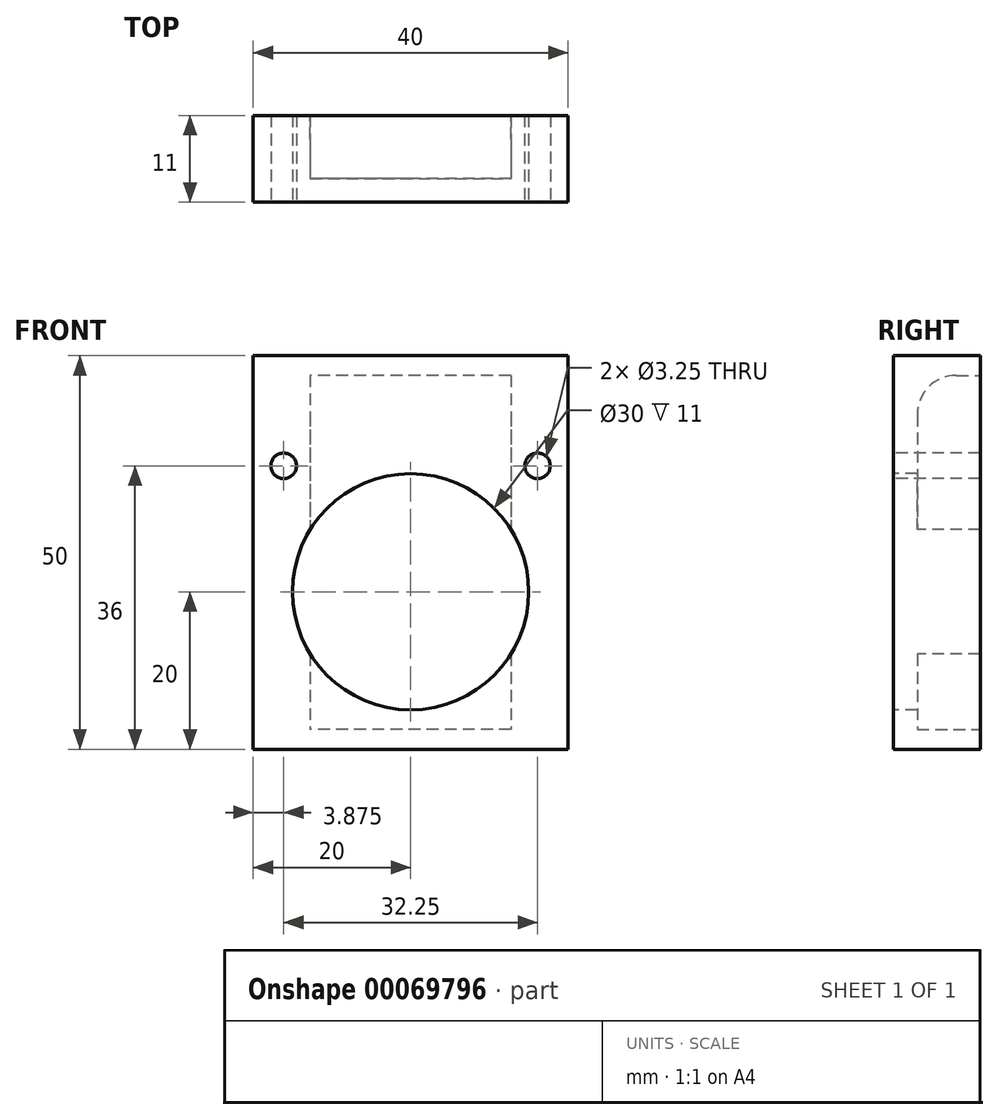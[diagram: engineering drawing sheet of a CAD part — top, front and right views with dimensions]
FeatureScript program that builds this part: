
annotation { "Feature Type Name" : "Feature", "Feature Type Description" : "" }
export const myFeature = defineFeature(function(context is Context, id is Id, definition is map)
    precondition{}
    {
        {
            var Q0;
            Q0=qCreatedBy(makeId("Front.planeOp"),FACE);
            var sketch = newSketch(context, id + "F0", { "sketchPlane" : qUnion([Q0])});
            skLineSegment(sketch, "E0.rect.bottom", {"start": v(-20, 25) * mm, "end": v(20, 25) * mm});
            skLineSegment(sketch, "E0.rect.top", {"start": v(-20, -25) * mm, "end": v(20, -25) * mm});
            skLineSegment(sketch, "E0.rect.left", {"start": v(-20, 25) * mm, "end": v(-20, -25) * mm});
            skLineSegment(sketch, "E0.rect.right", {"start": v(20, 25) * mm, "end": v(20, -25) * mm});
            skPoint(sketch, "E0.rect.middle", {"position": v(0, 0) * mm});
            skSolve(sketch);
        }
        {
            var Q0;
            Q0=makeQuery(id+"F0.imprint","IMPRINT",FACE,{"disambiguationData":[TD([[makeQuery(id+"F0.imprint","IMPRINT",EDGE,{"derivedFrom":sQuery(id+"F0.wireOp",EDGE,"E0.rect.bottom")}),-1.0]])]});
            extrude(context, id + "F1", {"entities" : qUnion([Q0]), "depth" : 11 * mm});
        }
        {
            var Q0;
            Q0=makeQuery(id+"F1.opExtrude","CAP_FACE",FACE,{"disambiguationData":[OSD([sQuery(id+"F0.wireOp",EDGE,"E0.rect.bottom"),sQuery(id+"F0.wireOp",EDGE,"E0.rect.top"),sQuery(id+"F0.wireOp",EDGE,"E0.rect.left"),sQuery(id+"F0.wireOp",EDGE,"E0.rect.right")])],"isStart":false});
            var sketch = newSketch(context, id + "F2", { "sketchPlane" : qUnion([Q0])});
            skCircle(sketch, "E1", {"center": v(-16.12, 11) * mm, "radius": 1.63 * mm});
            skCircle(sketch, "E2", {"center": v(16.12, 11) * mm, "radius": 1.63 * mm});
            skSolve(sketch);
        }
        {
            var Q0;
            Q0=makeQuery(id+"F2.imprint","IMPRINT",FACE,{"disambiguationData":[TD([[makeQuery(id+"F2.imprint","IMPRINT",EDGE,{"derivedFrom":sQuery(id+"F2.wireOp",EDGE,"E1")}),1.0]])]});
            var Q1;
            Q1=makeQuery(id+"F2.imprint","IMPRINT",FACE,{"disambiguationData":[TD([[makeQuery(id+"F2.imprint","IMPRINT",EDGE,{"derivedFrom":sQuery(id+"F2.wireOp",EDGE,"E2")}),1.0]])]});
            extrude(context, id + "F3", {"entities" : qUnion([Q0, Q1]), "operationType" : NewBodyOperationType.REMOVE, "endBound" : BoundingType.THROUGH_ALL, "oppositeDirection" : true, "depth" : 25 * mm});
        }
        {
            var Q0;
            Q0=makeQuery(id+"F1.opExtrude","CAP_FACE",FACE,{"disambiguationData":[OSD([sQuery(id+"F0.wireOp",EDGE,"E0.rect.bottom"),sQuery(id+"F0.wireOp",EDGE,"E0.rect.top"),sQuery(id+"F0.wireOp",EDGE,"E0.rect.left"),sQuery(id+"F0.wireOp",EDGE,"E0.rect.right")])],"isStart":true});
            var sketch = newSketch(context, id + "F4", { "sketchPlane" : qUnion([Q0])});
            skLineSegment(sketch, "E3.rect.bottom", {"start": v(-12.75, 22.5) * mm, "end": v(12.75, 22.5) * mm});
            skLineSegment(sketch, "E3.rect.top", {"start": v(-12.75, -22.5) * mm, "end": v(12.75, -22.5) * mm});
            skLineSegment(sketch, "E3.rect.left", {"start": v(-12.75, 22.5) * mm, "end": v(-12.75, -22.5) * mm});
            skLineSegment(sketch, "E3.rect.right", {"start": v(12.75, 22.5) * mm, "end": v(12.75, -22.5) * mm});
            skPoint(sketch, "E3.rect.middle", {"position": v(0, 0) * mm});
            skSolve(sketch);
        }
        {
            var Q0;
            Q0=makeQuery(id+"F4.imprint","IMPRINT",FACE,{"disambiguationData":[TD([[makeQuery(id+"F4.imprint","IMPRINT",EDGE,{"derivedFrom":sQuery(id+"F4.wireOp",EDGE,"E3.rect.bottom")}),-1.0]])]});
            extrude(context, id + "F5", {"entities" : qUnion([Q0]), "operationType" : NewBodyOperationType.REMOVE, "oppositeDirection" : true, "depth" : 8 * mm});
        }
        {
            var Q0;
            Q0=makeQuery(id+"F5.boolean.opBoolean","COPY",EDGE,{"derivedFrom":makeQuery(id+"F5.opExtrude","CAP_EDGE",EDGE,{"disambiguationData":[OSD([sQuery(id+"F4.wireOp",EDGE,"E3.rect.bottom")])],"isStart":false})});
            fillet(context, id + "F6", {"entities" : qUnion([Q0]), "radius" : 5 * mm, "tangentPropagation" : true, "allowEdgeOverflow" : false});
        }
        {
            var Q0;
            Q0=makeQuery(id+"F1.opExtrude","CAP_FACE",FACE,{"disambiguationData":[OSD([sQuery(id+"F0.wireOp",EDGE,"E0.rect.bottom"),sQuery(id+"F0.wireOp",EDGE,"E0.rect.top"),sQuery(id+"F0.wireOp",EDGE,"E0.rect.left"),sQuery(id+"F0.wireOp",EDGE,"E0.rect.right")])],"isStart":false});
            var sketch = newSketch(context, id + "F7", { "sketchPlane" : qUnion([Q0])});
            skCircle(sketch, "E4", {"center": v(0, -5) * mm, "radius": 15 * mm});
            skSolve(sketch);
        }
        {
            var Q0;
            Q0=makeQuery(id+"F7.imprint","IMPRINT",FACE,{"disambiguationData":[TD([[makeQuery(id+"F7.imprint","IMPRINT",EDGE,{"derivedFrom":sQuery(id+"F7.wireOp",EDGE,"E4")}),1.0]])]});
            extrude(context, id + "F8", {"entities" : qUnion([Q0]), "operationType" : NewBodyOperationType.REMOVE, "oppositeDirection" : true, "depth" : 25 * mm});
        }
    });
